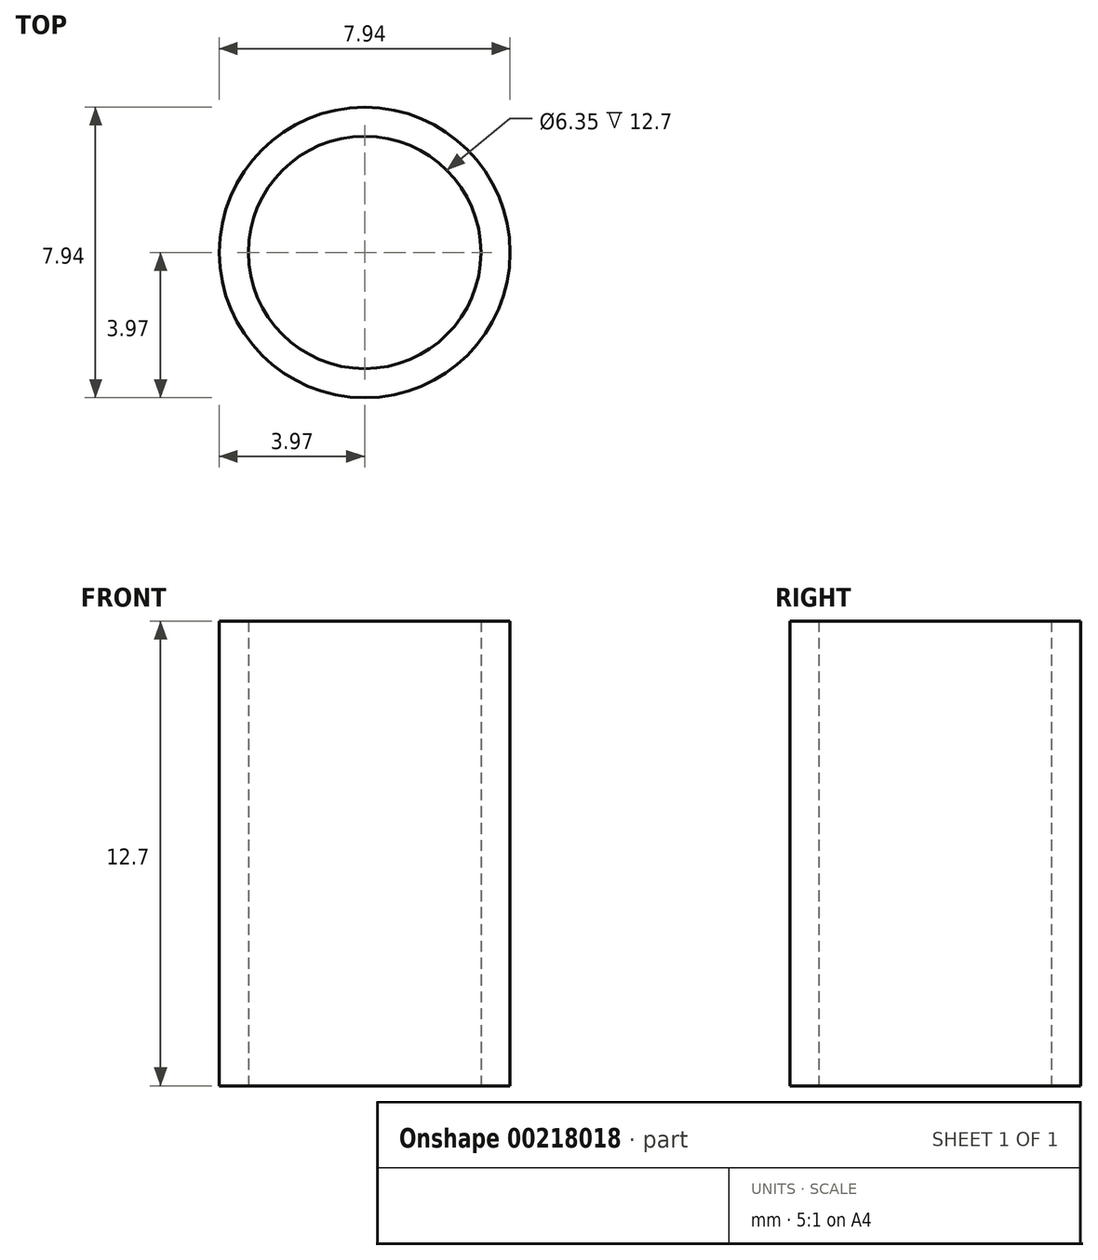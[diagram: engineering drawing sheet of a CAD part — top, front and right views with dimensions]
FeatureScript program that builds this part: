
annotation { "Feature Type Name" : "Feature", "Feature Type Description" : "" }
export const myFeature = defineFeature(function(context is Context, id is Id, definition is map)
    precondition{}
    {
        {
            var Q0;
            Q0=qCreatedBy(makeId("Top.planeOp"),FACE);
            var sketch = newSketch(context, id + "F0", { "sketchPlane" : qUnion([Q0])});
            skCircle(sketch, "E0", {"center": v(0, 0) * mm, "radius": 3.97 * mm});
            skCircle(sketch, "E1", {"center": v(0, 0) * mm, "radius": 3.18 * mm});
            skSolve(sketch);
        }
        {
            var Q0;
            Q0=qSketchRegion(id+"F0",true);
            extrude(context, id + "F1", {"entities" : qUnion([Q0]), "depth" : 12.7 * mm, "offsetDistance" : 25.4 * mm});
        }
    });
